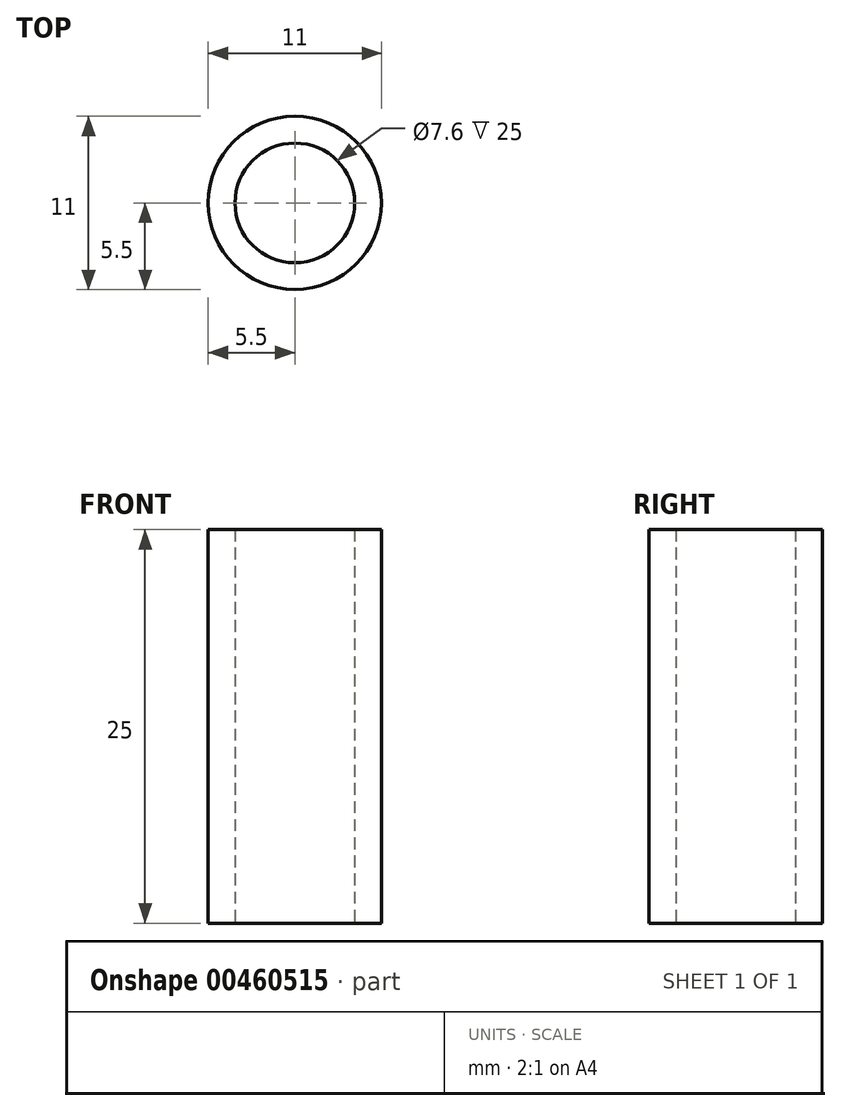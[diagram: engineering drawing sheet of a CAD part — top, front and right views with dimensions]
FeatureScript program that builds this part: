
annotation { "Feature Type Name" : "Feature", "Feature Type Description" : "" }
export const myFeature = defineFeature(function(context is Context, id is Id, definition is map)
    precondition{}
    {
        {
            var Q0;
            Q0=qCreatedBy(makeId("Top.planeOp"),FACE);
            var sketch = newSketch(context, id + "F0", { "sketchPlane" : qUnion([Q0])});
            skCircle(sketch, "E0", {"center": v(0, 0) * mm, "radius": 5.5 * mm});
            skCircle(sketch, "E1", {"center": v(0, 0) * mm, "radius": 3.8 * mm});
            skSolve(sketch);
        }
        {
            var Q0;
            Q0 = qSketchRegion(id + "F0", true);
            extrude(context, id + "F1", {"entities" : qUnion([Q0]), "depth" : 25 * mm});
        }
    });
